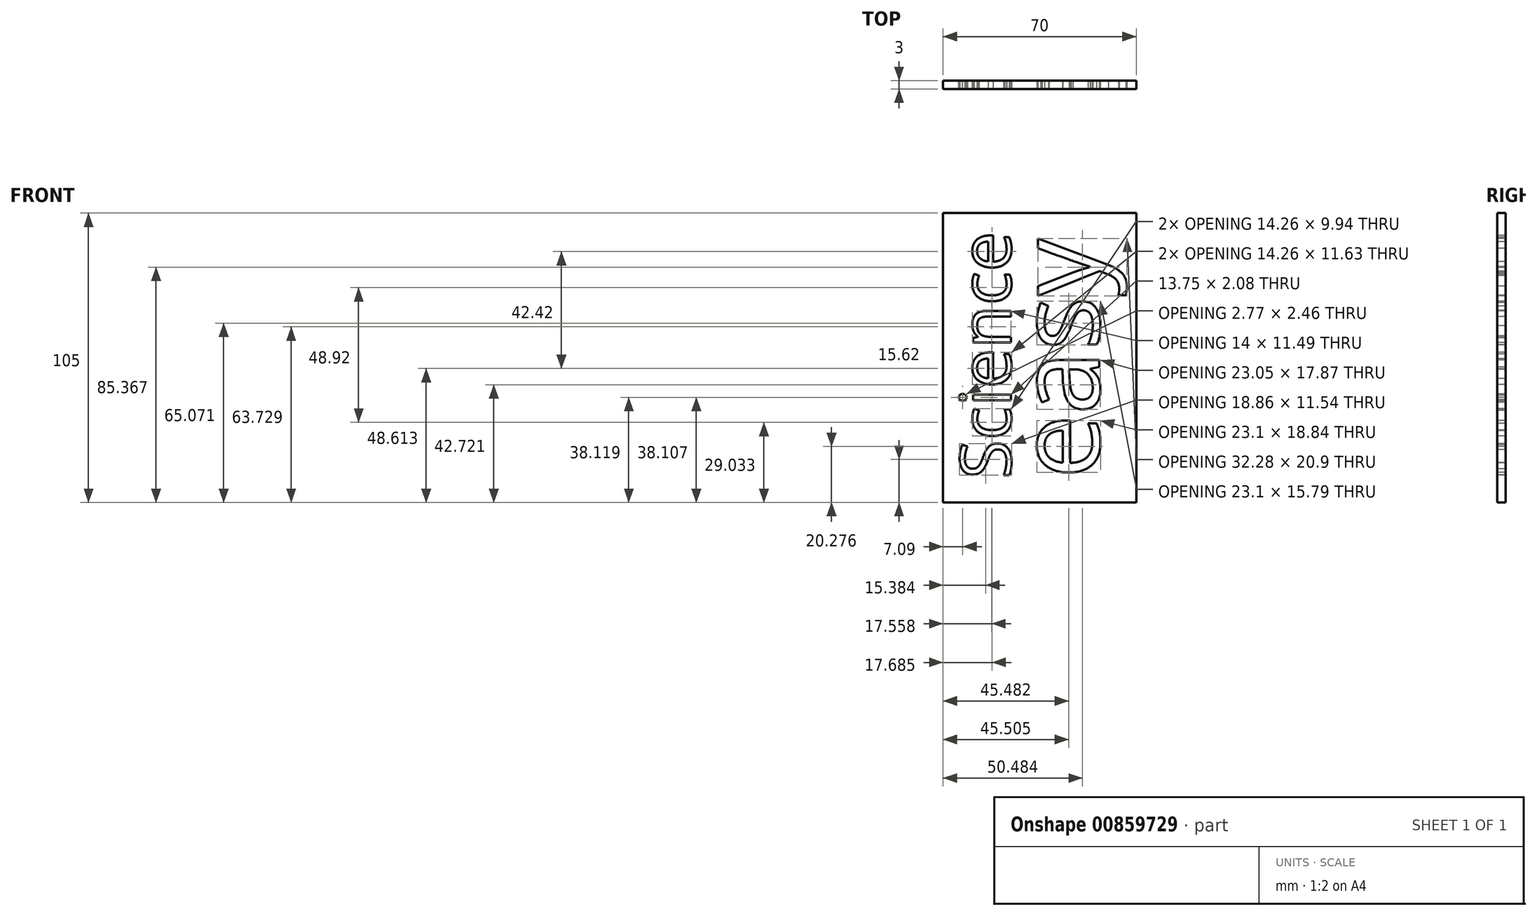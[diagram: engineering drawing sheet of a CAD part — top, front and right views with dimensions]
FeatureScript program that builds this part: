
annotation { "Feature Type Name" : "Feature", "Feature Type Description" : "" }
export const myFeature = defineFeature(function(context is Context, id is Id, definition is map)
    precondition{}
    {
        {
            var Q0;
            Q0=qCreatedBy(makeId("Front.planeOp"),FACE);
            var sketch = newSketch(context, id + "F0", { "sketchPlane" : qUnion([Q0])});
            skLineSegment(sketch, "E0.bottom", {"start": v(0, 0) * mm, "end": v(70, 0) * mm});
            skLineSegment(sketch, "E0.top", {"start": v(0, 105) * mm, "end": v(70, 105) * mm});
            skLineSegment(sketch, "E0.left", {"start": v(0, 0) * mm, "end": v(0, 105) * mm});
            skLineSegment(sketch, "E0.right", {"start": v(70, 0) * mm, "end": v(70, 105) * mm});
            skSolve(sketch);
        }
        {
            var Q0;
            Q0 = qSketchRegion(id + "F0", true);
            extrude(context, id + "F1", {"entities" : qUnion([Q0]), "depth" : 3 * mm, "offsetDistance" : 25.4 * mm});
        }
        {
            var Q0;
            Q0=makeQuery(id+"F1.opExtrude","CAP_FACE",FACE,{"disambiguationData":[OSD([sQuery(id+"F0.wireOp",EDGE,"E0.bottom"),sQuery(id+"F0.wireOp",EDGE,"E0.top"),sQuery(id+"F0.wireOp",EDGE,"E0.left"),sQuery(id+"F0.wireOp",EDGE,"E0.right")])],"isStart":false});
            var sketch = newSketch(context, id + "F2", { "sketchPlane" : qUnion([Q0])});
            skText(sketch, "E1", { "text": "Science", "fontName": "OpenSans-Regular.ttf"});
            skText(sketch, "E2", { "text": "easy", "fontName": "OpenSans-Regular.ttf"});
            const initialGuessF2  = {"E1": [0.02456, 0.00852, 0, 1, 0.0185], "E2": [0.05662, 0.00852, 0, 1, 0.02997]};
            skSetInitialGuess(sketch, initialGuessF2);
            skSolve(sketch);
        }
        {
            var Q0;
            Q0 = qSketchRegion(id + "F2", true);
            extrude(context, id + "F3", {"entities" : qUnion([Q0]), "operationType" : NewBodyOperationType.REMOVE, "oppositeDirection" : true, "depth" : 25.4 * mm, "offsetDistance" : 25.4 * mm});
        }
    });
